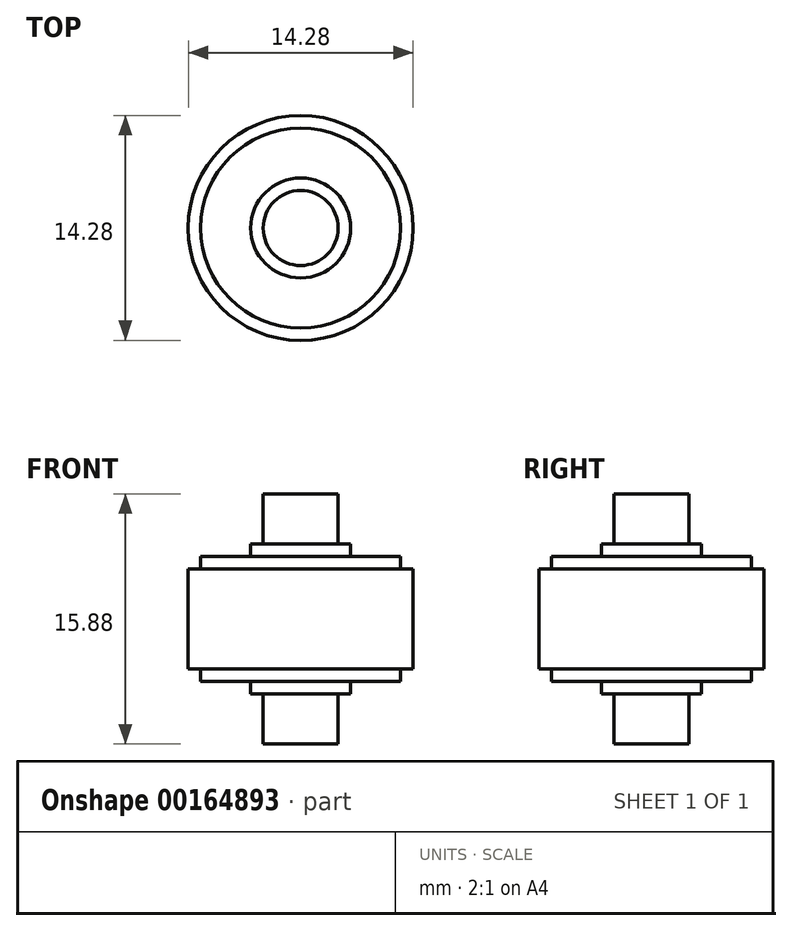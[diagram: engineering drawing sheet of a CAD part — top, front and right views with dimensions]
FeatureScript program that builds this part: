
annotation { "Feature Type Name" : "Feature", "Feature Type Description" : "" }
export const myFeature = defineFeature(function(context is Context, id is Id, definition is map)
    precondition{}
    {
        {
            var Q0;
            Q0=qCreatedBy(makeId("Top.planeOp"),FACE);
            var sketch = newSketch(context, id + "F0", { "sketchPlane" : qUnion([Q0])});
            skCircle(sketch, "E0", {"center": v(0, 0) * mm, "radius": 2.38 * mm});
            skSolve(sketch);
        }
        {
            var Q0;
            Q0 = qSketchRegion(id + "F0", true);
            extrude(context, id + "F1", {"entities" : qUnion([Q0]), "endBound" : BoundingType.SYMMETRIC, "depth" : 15.88 * mm});
        }
        {
            var Q0;
            Q0=qCreatedBy(makeId("Top.planeOp"),FACE);
            var sketch = newSketch(context, id + "F2", { "sketchPlane" : qUnion([Q0])});
            skCircle(sketch, "E1", {"center": v(0, 0) * mm, "radius": 3.18 * mm});
            skSolve(sketch);
        }
        {
            var Q0;
            Q0 = qSketchRegion(id + "F2", true);
            extrude(context, id + "F3", {"entities" : qUnion([Q0]), "operationType" : NewBodyOperationType.ADD, "endBound" : BoundingType.SYMMETRIC, "depth" : 9.52 * mm});
        }
        {
            var Q0;
            Q0=qCreatedBy(makeId("Top.planeOp"),FACE);
            var sketch = newSketch(context, id + "F4", { "sketchPlane" : qUnion([Q0])});
            skCircle(sketch, "E2", {"center": v(0, 0) * mm, "radius": 7.14 * mm});
            skSolve(sketch);
        }
        {
            var Q0;
            Q0 = qSketchRegion(id + "F4", true);
            extrude(context, id + "F5", {"entities" : qUnion([Q0]), "operationType" : NewBodyOperationType.ADD, "endBound" : BoundingType.SYMMETRIC, "depth" : 6.35 * mm});
        }
        {
            var Q0;
            Q0=qCreatedBy(makeId("Top.planeOp"),FACE);
            var sketch = newSketch(context, id + "F6", { "sketchPlane" : qUnion([Q0])});
            skCircle(sketch, "E3", {"center": v(0, 0) * mm, "radius": 6.35 * mm});
            skSolve(sketch);
        }
        {
            var Q0;
            Q0 = qSketchRegion(id + "F6", true);
            extrude(context, id + "F7", {"entities" : qUnion([Q0]), "operationType" : NewBodyOperationType.ADD, "endBound" : BoundingType.SYMMETRIC, "depth" : 7.94 * mm});
        }
    });
